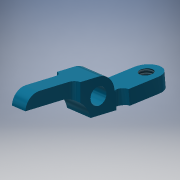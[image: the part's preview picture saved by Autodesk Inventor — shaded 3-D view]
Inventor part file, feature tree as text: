
AUTODESK INVENTOR PART (.ipt)
format: ipt  version: 2018 (Build 220112000, 112)  size: 203,264 bytes
history: native  units: mm
features: sketch x4, extrude x3, projected_geometry x3, thread x1, other x1, fillet x1
ambient origin geometry x8: Origin, YZ Plane, XZ Plane, XY Plane, X Axis, Y Axis, Z Axis, Center Point
bodies: Solid1 (feature_tree)
feature tree (13):
  extrude  "Extrusion1"  Depth=4.7mm
  extrude  "Extrusion2"  Depth=4.0mm
  extrude  "Extrusion3"  Depth=1.3mm
  thread  "Thread1"  [1 undecoded]
  other  "Bend Part1"
  fillet  "Fillet1"  Radius=3.5mm
  sketch  "Sketch1"  dims[d0=8.0mm d1=4.7mm]
  sketch  "Sketch2"  dims[d2=3.5mm d4=4.0mm]
  sketch  "Sketch3"  dims[d5=12.0mm d7=1.3mm d8=4.0mm d9=3.5mm]
  sketch  "Sketch4"  dims[d10=9.18mm d11=16.98mm d12=14.0mm d13=0.0mm d14=4.0mm d15=31.85mm d16=7.0mm d17=3.02mm d18=22.98mm d19=1.5mm d20=10.98mm d21=14.0mm d22=0.0mm d23=3.24mm d24=14.0mm d25=0.0mm d26=10.0mm d27=0.0mm d28=23.5mm d29=10.0mm d30=0.872665mm d31=1.0mm]
  projected_geometry  "Project Cut Edges1"
  projected_geometry  "Project Cut Edges2"
  projected_geometry  "Project Cut Edges3"
note: 1 required parameter value undecoded (feature->parameter linkage not recoverable at this tier; creation-order binding heuristic only, values carry confidence <= 0.55)
